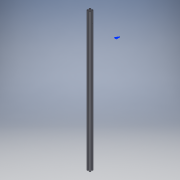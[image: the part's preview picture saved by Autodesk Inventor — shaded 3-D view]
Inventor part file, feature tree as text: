
AUTODESK INVENTOR PART (.ipt)
format: ipt  version: 2019 (Build 230136000, 136)  size: 316,416 bytes
history: native  units: in
note: dims shown in document units (in); Inventor stores cm internally (conversion verified against a paired STEP export)
features: extrude x1, sketch x1, projected_geometry x1
ambient origin geometry x8: Origin, YZ Plane, XZ Plane, XY Plane, X Axis, Y Axis, Z Axis, Center Point
bodies: Solid1 (feature_tree), Body1 (feature_tree)
feature tree (3):
  extrude  "Extrusion1"  [1 undecoded]
  sketch  "Sketch1"  dims[d0=35.4331in d1=0.0in]
  projected_geometry  "Projected Loop1"
note: 1 required parameter value undecoded (feature->parameter linkage not recoverable at this tier; creation-order binding heuristic only, values carry confidence <= 0.55)
